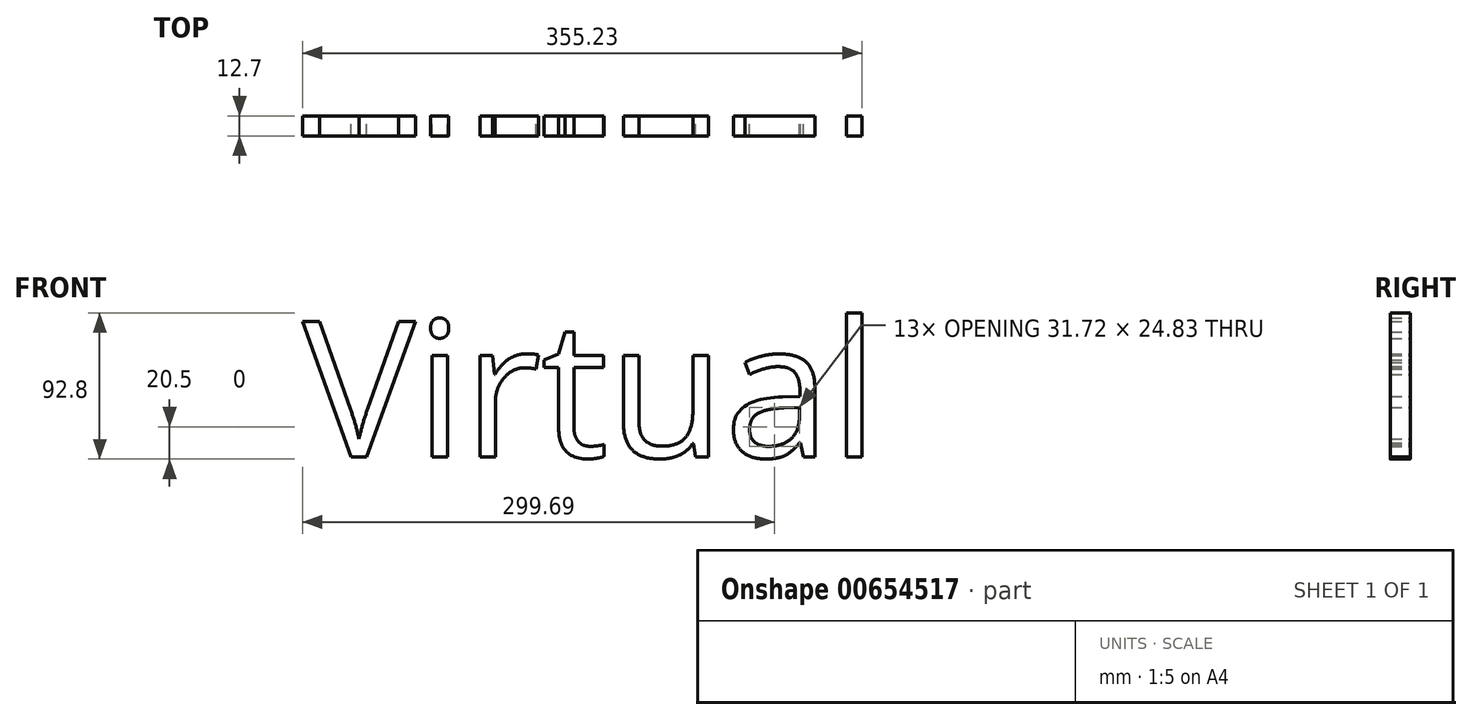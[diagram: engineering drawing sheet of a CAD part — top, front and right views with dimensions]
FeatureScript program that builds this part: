
annotation { "Feature Type Name" : "Feature", "Feature Type Description" : "" }
export const myFeature = defineFeature(function(context is Context, id is Id, definition is map)
    precondition{}
    {
        {
            var Q0;
            Q0=qCreatedBy(makeId("Front.planeOp"),FACE);
            var sketch = newSketch(context, id + "F0", { "sketchPlane" : qUnion([Q0])});
            skText(sketch, "E0", { "text": "Virtual", "fontName": "OpenSans-Regular.ttf"});
            const initialGuessF0  = {"E0": [-0.04676, -0.04456, 1, 0, 0.08681]};
            skSetInitialGuess(sketch, initialGuessF0);
            skSolve(sketch);
        }
        {
            var Q0;
            Q0 = qSketchRegion(id + "F0", true);
            extrude(context, id + "F1", {"entities" : qUnion([Q0]), "depth" : 12.7 * mm, "offsetDistance" : 25.4 * mm});
        }
    });
